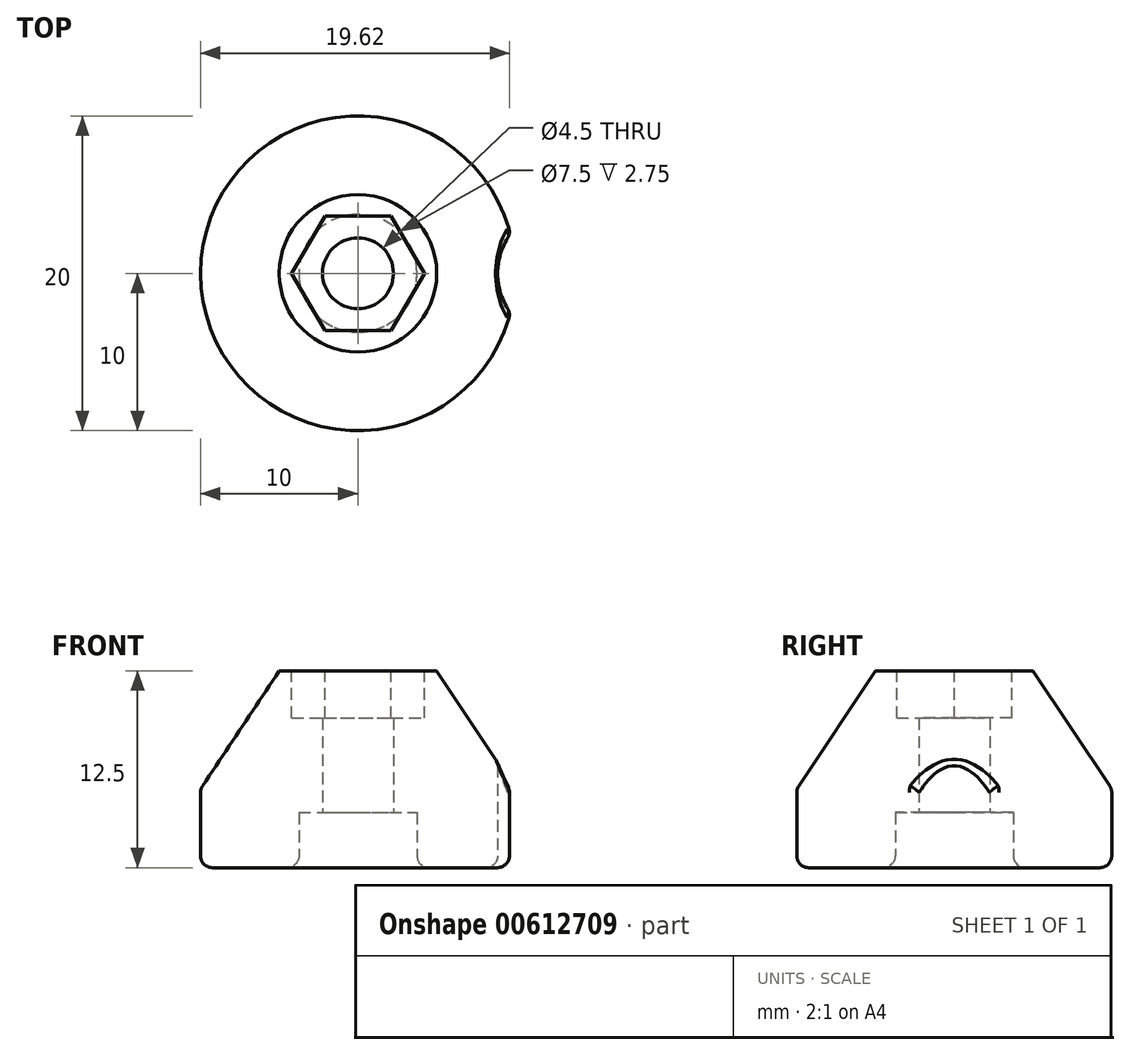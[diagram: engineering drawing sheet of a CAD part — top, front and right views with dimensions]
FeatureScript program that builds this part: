
annotation { "Feature Type Name" : "Feature", "Feature Type Description" : "" }
export const myFeature = defineFeature(function(context is Context, id is Id, definition is map)
    precondition{}
    {
        {
            var Q0;
            Q0=qCreatedBy(makeId("Front.planeOp"),FACE);
            var sketch = newSketch(context, id + "F0", { "sketchPlane" : qUnion([Q0])});
            skLineSegment(sketch, "E0", {"start": v(3.75, 3.5) * mm, "end": v(2.25, 3.5) * mm});
            skLineSegment(sketch, "E1", {"start": v(2.25, 3.5) * mm, "end": v(2.25, 12.5) * mm});
            skLineSegment(sketch, "E2", {"start": v(2.25, 12.5) * mm, "end": v(5, 12.5) * mm});
            skLineSegment(sketch, "E3", {"start": v(5, 12.5) * mm, "end": v(10, 5) * mm});
            skLineSegment(sketch, "E4", {"start": v(10, 5) * mm, "end": v(10, 0) * mm});
            skLineSegment(sketch, "E5", {"start": v(10, 0) * mm, "end": v(7.5, 0) * mm});
            skLineSegment(sketch, "E6", {"start": v(0, 0) * mm, "end": v(0, 22.04) * mm, "construction": true});
            skLineSegment(sketch, "E7", {"start": v(7.5, 0) * mm, "end": v(3.75, 0) * mm});
            skLineSegment(sketch, "E8", {"start": v(3.75, 3.5) * mm, "end": v(3.75, 0) * mm});
            skSolve(sketch);
        }
        {
            var Q0;
            Q0=makeQuery(id+"F0.imprint","IMPRINT",FACE,{"disambiguationData":[TD([[makeQuery(id+"F0.imprint","IMPRINT",EDGE,{"derivedFrom":sQuery(id+"F0.wireOp",EDGE,"E0")}),-1.0]])]});
            var Q1;
            Q1=sQuery(id+"F0.wireOp",EDGE,"E6");
            revolve(context, id + "F1", {"entities" : qUnion([Q0]), "axis" : qUnion([Q1]), "revolveType" : RevolveType.FULL});
        }
        {
            var Q0;
            Q0=makeQuery(id+"F1.opRevolve","SWEPT_FACE",FACE,{"disambiguationData":[OSD([sQuery(id+"F0.wireOp",EDGE,"E2")])]});
            var sketch = newSketch(context, id + "F2", { "sketchPlane" : qUnion([Q0])});
            skCircle(sketch, "E9.cCircle", {"center": v(0, 0) * mm, "radius": 3.65 * mm, "construction": true});
            skLineSegment(sketch, "E9.0", {"start": v(2.1, 3.65) * mm, "end": v(4.21, 0) * mm});
            skLineSegment(sketch, "E9.1", {"start": v(4.21, 0) * mm, "end": v(2.1, -3.65) * mm});
            skLineSegment(sketch, "E9.2", {"start": v(2.1, -3.65) * mm, "end": v(-2.1, -3.65) * mm});
            skLineSegment(sketch, "E9.3", {"start": v(-2.1, -3.65) * mm, "end": v(-4.21, 0) * mm});
            skLineSegment(sketch, "E9.4", {"start": v(-4.21, 0) * mm, "end": v(-2.1, 3.65) * mm});
            skLineSegment(sketch, "E9.5", {"start": v(-2.1, 3.65) * mm, "end": v(2.1, 3.65) * mm});
            skPoint(sketch, "E9.0.midPoint", {"position": v(3.16, 1.82) * mm});
            skSolve(sketch);
        }
        {
            var Q0;
            Q0=makeQuery(id+"F2.imprint","IMPRINT",FACE,{"disambiguationData":[TD([[makeQuery(id+"F2.imprint","IMPRINT",EDGE,{"derivedFrom":sQuery(id+"F2.wireOp",EDGE,"E9.0")}),-1.0]])]});
            extrude(context, id + "F3", {"entities" : qUnion([Q0]), "operationType" : NewBodyOperationType.REMOVE, "oppositeDirection" : true, "depth" : 3 * mm});
        }
        {
            var Q0;
            Q0=makeQuery(id+"F1.opRevolve","SWEPT_FACE",FACE,{"disambiguationData":[OSD([sQuery(id+"F0.wireOp",EDGE,"E5")])]});
            var sketch = newSketch(context, id + "F4", { "sketchPlane" : qUnion([Q0])});
            skCircle(sketch, "E10", {"center": v(13.12, 0) * mm, "radius": 4.25 * mm});
            skLineSegment(sketch, "E11", {"start": v(9.68, 2.5) * mm, "end": v(9.68, -2.5) * mm, "construction": true});
            skSolve(sketch);
        }
        {
            var Q0;
            {var subQ0=sQuery(id+"F4.wireOp",EDGE,"E10");var subQ1=makeQuery(id+"F1.opRevolve","SWEPT_EDGE",EDGE,{"disambiguationData":[OSD([sQuery(id+"F0.wireOp",EDGE,"E4"),sQuery(id+"F0.wireOp",EDGE,"E5")])]});var subQ2=makeQuery(id+"F4.imprint","INTERSECT",VERTEX,{"disambiguationData":[OD(0.0)],"derivedFrom":[subQ1,subQ0]});Q0=makeQuery(id+"F4.imprint","IMPRINT",FACE,{"disambiguationData":[TD([[makeQuery(id+"F4.imprint","IMPRINT",EDGE,{"disambiguationData":[TD([[subQ2,-1.0]])],"derivedFrom":subQ0}),1.0]])]});}
            extrude(context, id + "F5", {"entities" : qUnion([Q0]), "operationType" : NewBodyOperationType.REMOVE, "endBound" : BoundingType.THROUGH_ALL, "oppositeDirection" : true, "depth" : 25 * mm});
        }
        {
            var Q0;
            Q0=makeQuery(id+"F1.opRevolve","SWEPT_FACE",FACE,{"disambiguationData":[OSD([sQuery(id+"F0.wireOp",EDGE,"E5")])]});
            var Q1;
            Q1=makeQuery(id+"FlE0OcBPY4PQw9K_1.3.F5.boolean.opBoolean","COPY",FACE,{"derivedFrom":makeQuery(id+"FlE0OcBPY4PQw9K_1.3.F5.opExtrude","SWEPT_FACE",FACE,{"disambiguationData":[OSD([sQuery(id+"F4.wireOp",EDGE,"E10")])]})});
            var Q2;
            Q2=makeQuery(id+"FlE0OcBPY4PQw9K_1.2.F5.boolean.opBoolean","COPY",FACE,{"derivedFrom":makeQuery(id+"FlE0OcBPY4PQw9K_1.2.F5.opExtrude","SWEPT_FACE",FACE,{"disambiguationData":[OSD([sQuery(id+"F4.wireOp",EDGE,"E10")])]})});
            var Q3;
            Q3=makeQuery(id+"FlE0OcBPY4PQw9K_1.1.F5.boolean.opBoolean","COPY",FACE,{"derivedFrom":makeQuery(id+"FlE0OcBPY4PQw9K_1.1.F5.opExtrude","SWEPT_FACE",FACE,{"disambiguationData":[OSD([sQuery(id+"F4.wireOp",EDGE,"E10")])]})});
            var Q4;
            Q4=makeQuery(id+"F5.boolean.opBoolean","COPY",FACE,{"derivedFrom":makeQuery(id+"F5.opExtrude","SWEPT_FACE",FACE,{"disambiguationData":[OSD([sQuery(id+"F4.wireOp",EDGE,"E10")])]})});
            var Q5;
            Q5=makeQuery(id+"FlE0OcBPY4PQw9K_1.9.F5.boolean.opBoolean","COPY",FACE,{"derivedFrom":makeQuery(id+"FlE0OcBPY4PQw9K_1.9.F5.opExtrude","SWEPT_FACE",FACE,{"disambiguationData":[OSD([sQuery(id+"F4.wireOp",EDGE,"E10")])]})});
            var Q6;
            Q6=makeQuery(id+"FlE0OcBPY4PQw9K_1.8.F5.boolean.opBoolean","COPY",FACE,{"derivedFrom":makeQuery(id+"FlE0OcBPY4PQw9K_1.8.F5.opExtrude","SWEPT_FACE",FACE,{"disambiguationData":[OSD([sQuery(id+"F4.wireOp",EDGE,"E10")])]})});
            var Q7;
            Q7=makeQuery(id+"FlE0OcBPY4PQw9K_1.7.F5.boolean.opBoolean","COPY",FACE,{"derivedFrom":makeQuery(id+"FlE0OcBPY4PQw9K_1.7.F5.opExtrude","SWEPT_FACE",FACE,{"disambiguationData":[OSD([sQuery(id+"F4.wireOp",EDGE,"E10")])]})});
            var Q8;
            Q8=makeQuery(id+"FlE0OcBPY4PQw9K_1.6.F5.boolean.opBoolean","COPY",FACE,{"derivedFrom":makeQuery(id+"FlE0OcBPY4PQw9K_1.6.F5.opExtrude","SWEPT_FACE",FACE,{"disambiguationData":[OSD([sQuery(id+"F4.wireOp",EDGE,"E10")])]})});
            var Q9;
            Q9=makeQuery(id+"FlE0OcBPY4PQw9K_1.5.F5.boolean.opBoolean","COPY",FACE,{"derivedFrom":makeQuery(id+"FlE0OcBPY4PQw9K_1.5.F5.opExtrude","SWEPT_FACE",FACE,{"disambiguationData":[OSD([sQuery(id+"F4.wireOp",EDGE,"E10")])]})});
            var Q10;
            Q10=makeQuery(id+"FlE0OcBPY4PQw9K_1.4.F5.boolean.opBoolean","COPY",FACE,{"derivedFrom":makeQuery(id+"FlE0OcBPY4PQw9K_1.4.F5.opExtrude","SWEPT_FACE",FACE,{"disambiguationData":[OSD([sQuery(id+"F4.wireOp",EDGE,"E10")])]})});
            var Q11;
            {var subQ0=sQuery(id+"F0.wireOp",EDGE,"E3");var subQ2=sQuery(id+"F4.wireOp",EDGE,"E10");var subQ3=makeQuery(id+"F5.boolean.opBoolean","COPY",FACE,{"derivedFrom":makeQuery(id+"F5.opExtrude","SWEPT_FACE",FACE,{"disambiguationData":[OSD([subQ2])]})});var subQ4=sQuery(id+"F0.wireOp",EDGE,"E4");Q11=makeQuery(id+"FlE0OcBPY4PQw9K_1.9.F5.boolean.opBoolean","SPLIT",EDGE,{"disambiguationData":[TD([subQ3])],"derivedFrom":makeQuery(id+"FlE0OcBPY4PQw9K_1.8.F5.boolean.opBoolean","SPLIT",EDGE,{"disambiguationData":[TD([subQ3])],"derivedFrom":makeQuery(id+"FlE0OcBPY4PQw9K_1.7.F5.boolean.opBoolean","SPLIT",EDGE,{"disambiguationData":[TD([subQ3])],"derivedFrom":makeQuery(id+"FlE0OcBPY4PQw9K_1.6.F5.boolean.opBoolean","SPLIT",EDGE,{"disambiguationData":[TD([subQ3])],"derivedFrom":makeQuery(id+"FlE0OcBPY4PQw9K_1.5.F5.boolean.opBoolean","SPLIT",EDGE,{"disambiguationData":[TD([subQ3])],"derivedFrom":makeQuery(id+"FlE0OcBPY4PQw9K_1.4.F5.boolean.opBoolean","SPLIT",EDGE,{"disambiguationData":[TD([subQ3])],"derivedFrom":makeQuery(id+"FlE0OcBPY4PQw9K_1.3.F5.boolean.opBoolean","SPLIT",EDGE,{"disambiguationData":[TD([subQ3])],"derivedFrom":makeQuery(id+"FlE0OcBPY4PQw9K_1.2.F5.boolean.opBoolean","SPLIT",EDGE,{"disambiguationData":[TD([subQ3])],"derivedFrom":makeQuery(id+"FlE0OcBPY4PQw9K_1.1.F5.boolean.opBoolean","SPLIT",EDGE,{"disambiguationData":[OD(1.0)],"derivedFrom":makeQuery(id+"F1.opRevolve","SWEPT_EDGE",EDGE,{"disambiguationData":[OSD([subQ0,subQ4])]})})})})})})})})})});}
            var Q12;
            Q12=makeQuery(id+"FlE0OcBPY4PQw9K_1.1.F5.boolean.opBoolean","SPLIT",EDGE,{"disambiguationData":[OD(0.0)],"derivedFrom":makeQuery(id+"F1.opRevolve","SWEPT_EDGE",EDGE,{"disambiguationData":[OSD([sQuery(id+"F0.wireOp",EDGE,"E3"),sQuery(id+"F0.wireOp",EDGE,"E4")])]})});
            var Q13;
            {var subQ0=sQuery(id+"F0.wireOp",EDGE,"E3");var subQ1=sQuery(id+"F0.wireOp",EDGE,"E4");var subQ2=sQuery(id+"F4.wireOp",EDGE,"E10");Q13=makeQuery(id+"FlE0OcBPY4PQw9K_1.2.F5.boolean.opBoolean","SPLIT",EDGE,{"disambiguationData":[TD([makeQuery(id+"FlE0OcBPY4PQw9K_1.1.F5.boolean.opBoolean","COPY",FACE,{"derivedFrom":makeQuery(id+"FlE0OcBPY4PQw9K_1.1.F5.opExtrude","SWEPT_FACE",FACE,{"disambiguationData":[OSD([subQ2])]})})])],"derivedFrom":makeQuery(id+"FlE0OcBPY4PQw9K_1.1.F5.boolean.opBoolean","SPLIT",EDGE,{"disambiguationData":[OD(1.0)],"derivedFrom":makeQuery(id+"F1.opRevolve","SWEPT_EDGE",EDGE,{"disambiguationData":[OSD([subQ0,subQ1])]})})});}
            var Q14;
            {var subQ0=sQuery(id+"F0.wireOp",EDGE,"E3");var subQ2=sQuery(id+"F4.wireOp",EDGE,"E10");var subQ3=sQuery(id+"F0.wireOp",EDGE,"E4");var subQ5=makeQuery(id+"FlE0OcBPY4PQw9K_1.2.F5.opExtrude","SWEPT_FACE",FACE,{"disambiguationData":[OSD([subQ2])]});Q14=makeQuery(id+"FlE0OcBPY4PQw9K_1.3.F5.boolean.opBoolean","SPLIT",EDGE,{"disambiguationData":[TD([makeQuery(id+"FlE0OcBPY4PQw9K_1.2.F5.boolean.opBoolean","COPY",FACE,{"derivedFrom":subQ5})])],"derivedFrom":makeQuery(id+"FlE0OcBPY4PQw9K_1.2.F5.boolean.opBoolean","SPLIT",EDGE,{"disambiguationData":[TD([makeQuery(id+"F5.boolean.opBoolean","COPY",FACE,{"derivedFrom":makeQuery(id+"F5.opExtrude","SWEPT_FACE",FACE,{"disambiguationData":[OSD([subQ2])]})})])],"derivedFrom":makeQuery(id+"FlE0OcBPY4PQw9K_1.1.F5.boolean.opBoolean","SPLIT",EDGE,{"disambiguationData":[OD(1.0)],"derivedFrom":makeQuery(id+"F1.opRevolve","SWEPT_EDGE",EDGE,{"disambiguationData":[OSD([subQ0,subQ3])]})})})});}
            var Q15;
            {var subQ0=sQuery(id+"F0.wireOp",EDGE,"E3");var subQ2=sQuery(id+"F0.wireOp",EDGE,"E4");var subQ4=sQuery(id+"F4.wireOp",EDGE,"E10");var subQ5=makeQuery(id+"FlE0OcBPY4PQw9K_1.3.F5.opExtrude","SWEPT_FACE",FACE,{"disambiguationData":[OSD([subQ4])]});var subQ6=makeQuery(id+"F5.boolean.opBoolean","COPY",FACE,{"derivedFrom":makeQuery(id+"F5.opExtrude","SWEPT_FACE",FACE,{"disambiguationData":[OSD([subQ4])]})});Q15=makeQuery(id+"FlE0OcBPY4PQw9K_1.4.F5.boolean.opBoolean","SPLIT",EDGE,{"disambiguationData":[TD([makeQuery(id+"FlE0OcBPY4PQw9K_1.3.F5.boolean.opBoolean","COPY",FACE,{"derivedFrom":subQ5})])],"derivedFrom":makeQuery(id+"FlE0OcBPY4PQw9K_1.3.F5.boolean.opBoolean","SPLIT",EDGE,{"disambiguationData":[TD([subQ6])],"derivedFrom":makeQuery(id+"FlE0OcBPY4PQw9K_1.2.F5.boolean.opBoolean","SPLIT",EDGE,{"disambiguationData":[TD([subQ6])],"derivedFrom":makeQuery(id+"FlE0OcBPY4PQw9K_1.1.F5.boolean.opBoolean","SPLIT",EDGE,{"disambiguationData":[OD(1.0)],"derivedFrom":makeQuery(id+"F1.opRevolve","SWEPT_EDGE",EDGE,{"disambiguationData":[OSD([subQ0,subQ2])]})})})})});}
            var Q16;
            {var subQ0=sQuery(id+"F0.wireOp",EDGE,"E3");var subQ2=sQuery(id+"F0.wireOp",EDGE,"E4");var subQ4=sQuery(id+"F4.wireOp",EDGE,"E10");var subQ5=makeQuery(id+"FlE0OcBPY4PQw9K_1.4.F5.opExtrude","SWEPT_FACE",FACE,{"disambiguationData":[OSD([subQ4])]});var subQ6=makeQuery(id+"F5.boolean.opBoolean","COPY",FACE,{"derivedFrom":makeQuery(id+"F5.opExtrude","SWEPT_FACE",FACE,{"disambiguationData":[OSD([subQ4])]})});Q16=makeQuery(id+"FlE0OcBPY4PQw9K_1.5.F5.boolean.opBoolean","SPLIT",EDGE,{"disambiguationData":[TD([makeQuery(id+"FlE0OcBPY4PQw9K_1.4.F5.boolean.opBoolean","COPY",FACE,{"derivedFrom":subQ5})])],"derivedFrom":makeQuery(id+"FlE0OcBPY4PQw9K_1.4.F5.boolean.opBoolean","SPLIT",EDGE,{"disambiguationData":[TD([subQ6])],"derivedFrom":makeQuery(id+"FlE0OcBPY4PQw9K_1.3.F5.boolean.opBoolean","SPLIT",EDGE,{"disambiguationData":[TD([subQ6])],"derivedFrom":makeQuery(id+"FlE0OcBPY4PQw9K_1.2.F5.boolean.opBoolean","SPLIT",EDGE,{"disambiguationData":[TD([subQ6])],"derivedFrom":makeQuery(id+"FlE0OcBPY4PQw9K_1.1.F5.boolean.opBoolean","SPLIT",EDGE,{"disambiguationData":[OD(1.0)],"derivedFrom":makeQuery(id+"F1.opRevolve","SWEPT_EDGE",EDGE,{"disambiguationData":[OSD([subQ0,subQ2])]})})})})})});}
            var Q17;
            {var subQ0=sQuery(id+"F0.wireOp",EDGE,"E3");var subQ2=sQuery(id+"F4.wireOp",EDGE,"E10");var subQ3=makeQuery(id+"FlE0OcBPY4PQw9K_1.5.F5.opExtrude","SWEPT_FACE",FACE,{"disambiguationData":[OSD([subQ2])]});var subQ4=sQuery(id+"F0.wireOp",EDGE,"E4");var subQ6=makeQuery(id+"F5.boolean.opBoolean","COPY",FACE,{"derivedFrom":makeQuery(id+"F5.opExtrude","SWEPT_FACE",FACE,{"disambiguationData":[OSD([subQ2])]})});Q17=makeQuery(id+"FlE0OcBPY4PQw9K_1.6.F5.boolean.opBoolean","SPLIT",EDGE,{"disambiguationData":[TD([makeQuery(id+"FlE0OcBPY4PQw9K_1.5.F5.boolean.opBoolean","COPY",FACE,{"derivedFrom":subQ3})])],"derivedFrom":makeQuery(id+"FlE0OcBPY4PQw9K_1.5.F5.boolean.opBoolean","SPLIT",EDGE,{"disambiguationData":[TD([subQ6])],"derivedFrom":makeQuery(id+"FlE0OcBPY4PQw9K_1.4.F5.boolean.opBoolean","SPLIT",EDGE,{"disambiguationData":[TD([subQ6])],"derivedFrom":makeQuery(id+"FlE0OcBPY4PQw9K_1.3.F5.boolean.opBoolean","SPLIT",EDGE,{"disambiguationData":[TD([subQ6])],"derivedFrom":makeQuery(id+"FlE0OcBPY4PQw9K_1.2.F5.boolean.opBoolean","SPLIT",EDGE,{"disambiguationData":[TD([subQ6])],"derivedFrom":makeQuery(id+"FlE0OcBPY4PQw9K_1.1.F5.boolean.opBoolean","SPLIT",EDGE,{"disambiguationData":[OD(1.0)],"derivedFrom":makeQuery(id+"F1.opRevolve","SWEPT_EDGE",EDGE,{"disambiguationData":[OSD([subQ0,subQ4])]})})})})})})});}
            var Q18;
            {var subQ0=sQuery(id+"F0.wireOp",EDGE,"E3");var subQ2=sQuery(id+"F0.wireOp",EDGE,"E4");var subQ4=sQuery(id+"F4.wireOp",EDGE,"E10");var subQ5=makeQuery(id+"FlE0OcBPY4PQw9K_1.6.F5.opExtrude","SWEPT_FACE",FACE,{"disambiguationData":[OSD([subQ4])]});var subQ6=makeQuery(id+"F5.boolean.opBoolean","COPY",FACE,{"derivedFrom":makeQuery(id+"F5.opExtrude","SWEPT_FACE",FACE,{"disambiguationData":[OSD([subQ4])]})});Q18=makeQuery(id+"FlE0OcBPY4PQw9K_1.7.F5.boolean.opBoolean","SPLIT",EDGE,{"disambiguationData":[TD([makeQuery(id+"FlE0OcBPY4PQw9K_1.6.F5.boolean.opBoolean","COPY",FACE,{"derivedFrom":subQ5})])],"derivedFrom":makeQuery(id+"FlE0OcBPY4PQw9K_1.6.F5.boolean.opBoolean","SPLIT",EDGE,{"disambiguationData":[TD([subQ6])],"derivedFrom":makeQuery(id+"FlE0OcBPY4PQw9K_1.5.F5.boolean.opBoolean","SPLIT",EDGE,{"disambiguationData":[TD([subQ6])],"derivedFrom":makeQuery(id+"FlE0OcBPY4PQw9K_1.4.F5.boolean.opBoolean","SPLIT",EDGE,{"disambiguationData":[TD([subQ6])],"derivedFrom":makeQuery(id+"FlE0OcBPY4PQw9K_1.3.F5.boolean.opBoolean","SPLIT",EDGE,{"disambiguationData":[TD([subQ6])],"derivedFrom":makeQuery(id+"FlE0OcBPY4PQw9K_1.2.F5.boolean.opBoolean","SPLIT",EDGE,{"disambiguationData":[TD([subQ6])],"derivedFrom":makeQuery(id+"FlE0OcBPY4PQw9K_1.1.F5.boolean.opBoolean","SPLIT",EDGE,{"disambiguationData":[OD(1.0)],"derivedFrom":makeQuery(id+"F1.opRevolve","SWEPT_EDGE",EDGE,{"disambiguationData":[OSD([subQ0,subQ2])]})})})})})})})});}
            var Q19;
            {var subQ1=sQuery(id+"F4.wireOp",EDGE,"E10");var subQ3=makeQuery(id+"FlE0OcBPY4PQw9K_1.7.F5.opExtrude","SWEPT_FACE",FACE,{"disambiguationData":[OSD([subQ1])]});var subQ4=makeQuery(id+"F5.boolean.opBoolean","COPY",FACE,{"derivedFrom":makeQuery(id+"F5.opExtrude","SWEPT_FACE",FACE,{"disambiguationData":[OSD([subQ1])]})});Q19=makeQuery(id+"FlE0OcBPY4PQw9K_1.8.F5.boolean.opBoolean","SPLIT",FACE,{"disambiguationData":[TD([makeQuery(id+"FlE0OcBPY4PQw9K_1.7.F5.boolean.opBoolean","COPY",FACE,{"derivedFrom":subQ3})])],"derivedFrom":makeQuery(id+"FlE0OcBPY4PQw9K_1.7.F5.boolean.opBoolean","SPLIT",FACE,{"disambiguationData":[TD([subQ4])],"derivedFrom":makeQuery(id+"FlE0OcBPY4PQw9K_1.6.F5.boolean.opBoolean","SPLIT",FACE,{"disambiguationData":[TD([subQ4])],"derivedFrom":makeQuery(id+"FlE0OcBPY4PQw9K_1.5.F5.boolean.opBoolean","SPLIT",FACE,{"disambiguationData":[TD([subQ4])],"derivedFrom":makeQuery(id+"FlE0OcBPY4PQw9K_1.4.F5.boolean.opBoolean","SPLIT",FACE,{"disambiguationData":[TD([subQ4])],"derivedFrom":makeQuery(id+"FlE0OcBPY4PQw9K_1.3.F5.boolean.opBoolean","SPLIT",FACE,{"disambiguationData":[TD([subQ4])],"derivedFrom":makeQuery(id+"FlE0OcBPY4PQw9K_1.2.F5.boolean.opBoolean","SPLIT",FACE,{"disambiguationData":[TD([subQ4])],"derivedFrom":makeQuery(id+"FlE0OcBPY4PQw9K_1.1.F5.boolean.opBoolean","SPLIT",FACE,{"disambiguationData":[OD(1.0)],"derivedFrom":makeQuery(id+"F1.opRevolve","SWEPT_FACE",FACE,{"disambiguationData":[OSD([sQuery(id+"F0.wireOp",EDGE,"E4")])]})})})})})})})})});}
            var Q20;
            {var subQ0=sQuery(id+"F0.wireOp",EDGE,"E3");var subQ2=sQuery(id+"F0.wireOp",EDGE,"E4");var subQ4=sQuery(id+"F4.wireOp",EDGE,"E10");var subQ5=makeQuery(id+"FlE0OcBPY4PQw9K_1.8.F5.opExtrude","SWEPT_FACE",FACE,{"disambiguationData":[OSD([subQ4])]});var subQ6=makeQuery(id+"F5.boolean.opBoolean","COPY",FACE,{"derivedFrom":makeQuery(id+"F5.opExtrude","SWEPT_FACE",FACE,{"disambiguationData":[OSD([subQ4])]})});Q20=makeQuery(id+"FlE0OcBPY4PQw9K_1.9.F5.boolean.opBoolean","SPLIT",EDGE,{"disambiguationData":[TD([makeQuery(id+"FlE0OcBPY4PQw9K_1.8.F5.boolean.opBoolean","COPY",FACE,{"derivedFrom":subQ5})])],"derivedFrom":makeQuery(id+"FlE0OcBPY4PQw9K_1.8.F5.boolean.opBoolean","SPLIT",EDGE,{"disambiguationData":[TD([subQ6])],"derivedFrom":makeQuery(id+"FlE0OcBPY4PQw9K_1.7.F5.boolean.opBoolean","SPLIT",EDGE,{"disambiguationData":[TD([subQ6])],"derivedFrom":makeQuery(id+"FlE0OcBPY4PQw9K_1.6.F5.boolean.opBoolean","SPLIT",EDGE,{"disambiguationData":[TD([subQ6])],"derivedFrom":makeQuery(id+"FlE0OcBPY4PQw9K_1.5.F5.boolean.opBoolean","SPLIT",EDGE,{"disambiguationData":[TD([subQ6])],"derivedFrom":makeQuery(id+"FlE0OcBPY4PQw9K_1.4.F5.boolean.opBoolean","SPLIT",EDGE,{"disambiguationData":[TD([subQ6])],"derivedFrom":makeQuery(id+"FlE0OcBPY4PQw9K_1.3.F5.boolean.opBoolean","SPLIT",EDGE,{"disambiguationData":[TD([subQ6])],"derivedFrom":makeQuery(id+"FlE0OcBPY4PQw9K_1.2.F5.boolean.opBoolean","SPLIT",EDGE,{"disambiguationData":[TD([subQ6])],"derivedFrom":makeQuery(id+"FlE0OcBPY4PQw9K_1.1.F5.boolean.opBoolean","SPLIT",EDGE,{"disambiguationData":[OD(1.0)],"derivedFrom":makeQuery(id+"F1.opRevolve","SWEPT_EDGE",EDGE,{"disambiguationData":[OSD([subQ0,subQ2])]})})})})})})})})})});}
            fillet(context, id + "F6", {"entities" : qUnion([Q0, Q1, Q2, Q3, Q4, Q5, Q6, Q7, Q8, Q9, Q10, Q11, Q12, Q13, Q14, Q15, Q16, Q17, Q18, Q19, Q20]), "radius" : 0.75 * mm, "tangentPropagation" : true, "allowEdgeOverflow" : false});
        }
    });
